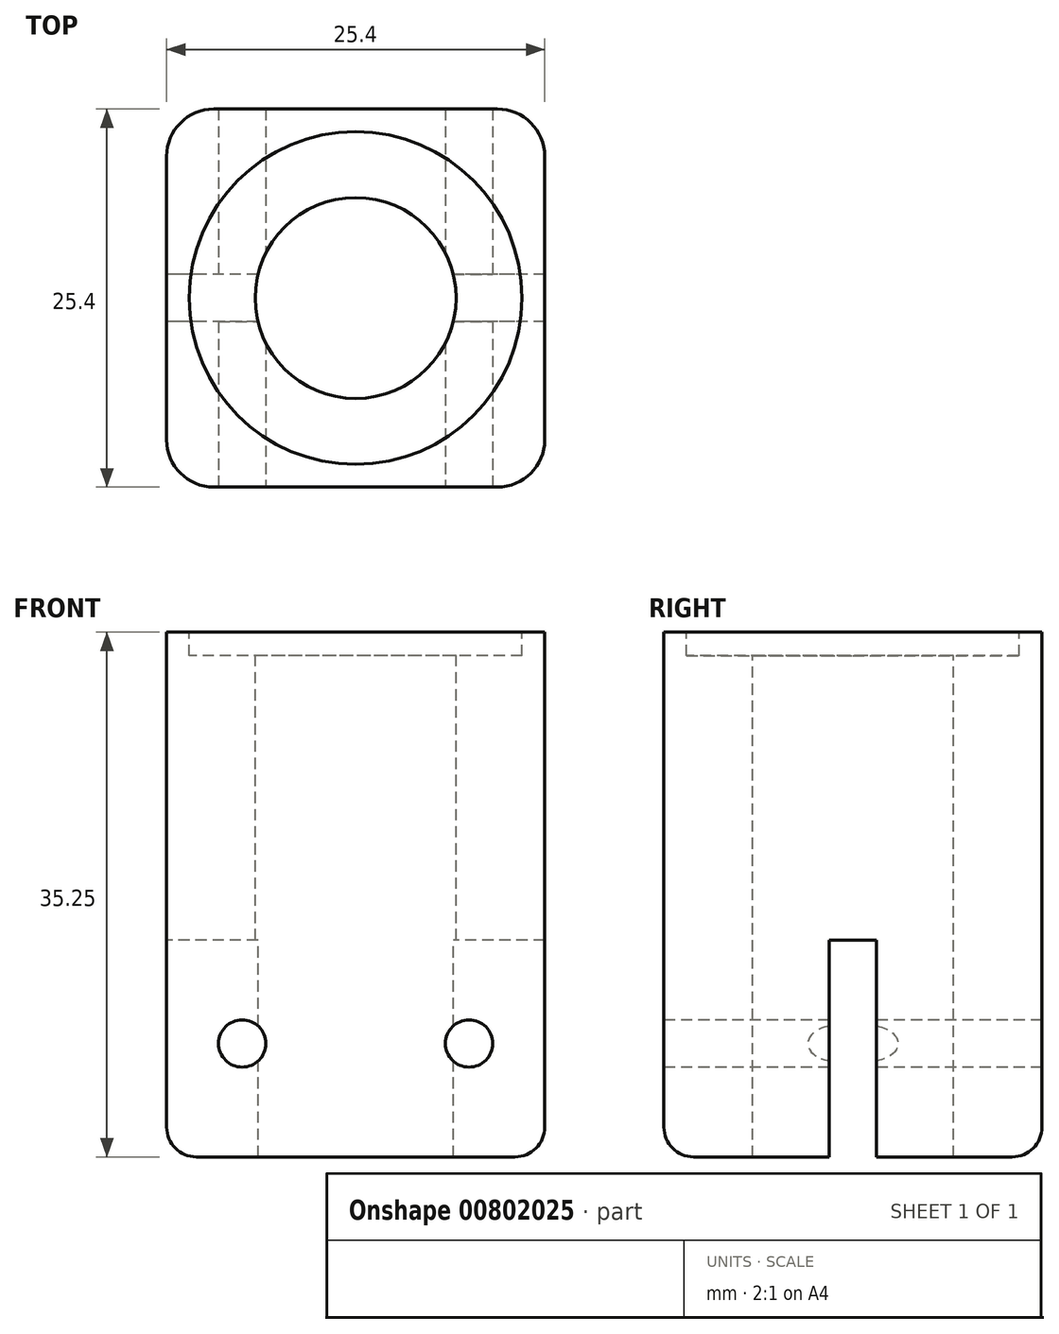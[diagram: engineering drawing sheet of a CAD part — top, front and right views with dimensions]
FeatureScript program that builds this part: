
annotation { "Feature Type Name" : "Feature", "Feature Type Description" : "" }
export const myFeature = defineFeature(function(context is Context, id is Id, definition is map)
    precondition{}
    {
        {
            var Q0;
            Q0=qCreatedBy(makeId("Top.planeOp"),FACE);
            var sketch = newSketch(context, id + "F0", { "sketchPlane" : qUnion([Q0])});
            skLineSegment(sketch, "E0.bottom", {"start": v(-9.52, 12.7) * mm, "end": v(9.52, 12.7) * mm});
            skLineSegment(sketch, "E0.top", {"start": v(-9.52, -12.7) * mm, "end": v(9.52, -12.7) * mm});
            skLineSegment(sketch, "E0.left", {"start": v(-12.7, 9.52) * mm, "end": v(-12.7, -9.53) * mm});
            skLineSegment(sketch, "E0.right", {"start": v(12.7, 9.52) * mm, "end": v(12.7, -9.53) * mm});
            skPoint(sketch, "E1.visualSharp", {"position": v(-12.7, 12.7) * mm});
            skArc(sketch, "E1.filletArc", {"start": v(-9.52, 12.7) * mm, "mid": v(-11.77, 11.77) * mm, "end": v(-12.7, 9.52) * mm});
            skPoint(sketch, "E2.visualSharp", {"position": v(12.7, 12.7) * mm});
            skArc(sketch, "E2.filletArc", {"start": v(12.7, 9.52) * mm, "mid": v(11.77, 11.77) * mm, "end": v(9.52, 12.7) * mm});
            skPoint(sketch, "E3.visualSharp", {"position": v(12.7, -12.7) * mm});
            skArc(sketch, "E3.filletArc", {"start": v(9.52, -12.7) * mm, "mid": v(11.77, -11.77) * mm, "end": v(12.7, -9.53) * mm});
            skPoint(sketch, "E4.visualSharp", {"position": v(-12.7, -12.7) * mm});
            skArc(sketch, "E4.filletArc", {"start": v(-12.7, -9.53) * mm, "mid": v(-11.77, -11.77) * mm, "end": v(-9.52, -12.7) * mm});
            skSolve(sketch);
        }
        {
            var Q0;
            Q0=qSketchRegion(id+"F0",true);
            extrude(context, id + "F1", {"entities" : qUnion([Q0]), "depth" : 36.1 * mm});
        }
        {
            var Q0;
            Q0=makeQuery(id+"F1.opExtrude","CAP_FACE",FACE,{"disambiguationData":[OSD([sQuery(id+"F0.wireOp",EDGE,"E0.bottom"),sQuery(id+"F0.wireOp",EDGE,"E0.top"),sQuery(id+"F0.wireOp",EDGE,"E0.left"),sQuery(id+"F0.wireOp",EDGE,"E0.right"),sQuery(id+"F0.wireOp",EDGE,"E1.filletArc"),sQuery(id+"F0.wireOp",EDGE,"E2.filletArc"),sQuery(id+"F0.wireOp",EDGE,"E3.filletArc"),sQuery(id+"F0.wireOp",EDGE,"E4.filletArc")])],"isStart":false});
            var sketch = newSketch(context, id + "F2", { "sketchPlane" : qUnion([Q0])});
            skPoint(sketch, "E5", {"position": v(0, 0) * mm});
            skSolve(sketch);
        }
        {
            var Q0;
            Q0=sQuery(id+"F2.wireOp",VERTEX,"E5");
            var Q1;
            Q1=makeQuery(id+"F1.opExtrude","SWEPT_BODY",BODY,{"disambiguationData":[OSD([sQuery(id+"F0.wireOp",EDGE,"E0.bottom"),sQuery(id+"F0.wireOp",EDGE,"E0.top"),sQuery(id+"F0.wireOp",EDGE,"E0.left"),sQuery(id+"F0.wireOp",EDGE,"E0.right"),sQuery(id+"F0.wireOp",EDGE,"E1.filletArc"),sQuery(id+"F0.wireOp",EDGE,"E2.filletArc"),sQuery(id+"F0.wireOp",EDGE,"E3.filletArc"),sQuery(id+"F0.wireOp",EDGE,"E4.filletArc")])]});
            hole(context, id + "F3", {"style" : HoleStyle.SIMPLE, "endStyle" : HoleEndStyle.THROUGH, "standardTappedOrClearance" : lookupTablePath({ "standard" : "ANSI", "engagement" : "75%", "pitch" : "11 tpi", "size" : "5/8", "type" : "Tapped" }), "standardBlindInLast" : lookupTablePath({ "standard" : "ANSI", "engagement" : "75%", "pitch" : "11 tpi", "size" : "5/8", "type" : "Tapped" }), "holeDiameter" : 13.5 * mm, "showTappedDepth" : true, "tappedDepth" : 19.05 * mm, "tapClearance" : 3, "startFromSketch" : true, "locations" : qUnion([Q0]), "scope" : qUnion([Q1]), "majorDiameter" : 15.88 * mm});
        }
        {
            var Q0;
            Q0=makeQuery(id+"F1.opExtrude","CAP_FACE",FACE,{"disambiguationData":[OSD([sQuery(id+"F0.wireOp",EDGE,"E0.bottom"),sQuery(id+"F0.wireOp",EDGE,"E0.top"),sQuery(id+"F0.wireOp",EDGE,"E0.left"),sQuery(id+"F0.wireOp",EDGE,"E0.right"),sQuery(id+"F0.wireOp",EDGE,"E1.filletArc"),sQuery(id+"F0.wireOp",EDGE,"E2.filletArc"),sQuery(id+"F0.wireOp",EDGE,"E3.filletArc"),sQuery(id+"F0.wireOp",EDGE,"E4.filletArc")])],"isStart":false});
            var sketch = newSketch(context, id + "F4", { "sketchPlane" : qUnion([Q0])});
            skCircle(sketch, "E6", {"center": v(0, 0) * mm, "radius": 11.18 * mm});
            skSolve(sketch);
        }
        {
            var Q0;
            Q0=qSketchRegion(id+"F4",true);
            extrude(context, id + "F5", {"entities" : qUnion([Q0]), "operationType" : NewBodyOperationType.REMOVE, "oppositeDirection" : true, "depth" : 1.59 * mm});
        }
        {
            var Q0;
            Q0=makeQuery(id+"F1.opExtrude","SWEPT_FACE",FACE,{"disambiguationData":[OSD([sQuery(id+"F0.wireOp",EDGE,"E0.left")])]});
            var sketch = newSketch(context, id + "F6", { "sketchPlane" : qUnion([Q0])});
            skLineSegment(sketch, "E7", {"start": v(0, 0) * mm, "end": v(0, 15.46) * mm, "construction": true});
            skPoint(sketch, "E8", {"position": v(0, 15.46) * mm});
            skLineSegment(sketch, "E9", {"start": v(0, 15.46) * mm, "end": v(1.59, 15.46) * mm});
            skLineSegment(sketch, "E10", {"start": v(1.59, 15.46) * mm, "end": v(1.59, -1.38) * mm});
            skLineSegment(sketch, "E11", {"start": v(0, 15.46) * mm, "end": v(-1.59, 15.46) * mm});
            skLineSegment(sketch, "E12", {"start": v(-1.59, 15.46) * mm, "end": v(-1.59, -0.8) * mm});
            skLineSegment(sketch, "E13", {"start": v(-1.59, -0.8) * mm, "end": v(1.59, -1.38) * mm});
            skSolve(sketch);
        }
        {
            var Q0;
            Q0=qSketchRegion(id+"F6",true);
            extrude(context, id + "F7", {"entities" : qUnion([Q0]), "operationType" : NewBodyOperationType.REMOVE, "endBound" : BoundingType.THROUGH_ALL, "oppositeDirection" : true, "depth" : 25.4 * mm});
        }
        {
            var Q0;
            Q0=makeQuery(id+"F1.opExtrude","SWEPT_FACE",FACE,{"disambiguationData":[OSD([sQuery(id+"F0.wireOp",EDGE,"E0.top")])]});
            var sketch = newSketch(context, id + "F8", { "sketchPlane" : qUnion([Q0])});
            skCircle(sketch, "E14", {"center": v(-7.62, 7.62) * mm, "radius": 1.59 * mm});
            skCircle(sketch, "E15", {"center": v(7.62, 7.62) * mm, "radius": 1.59 * mm});
            skSolve(sketch);
        }
        {
            var Q0;
            Q0=qSketchRegion(id+"F8",true);
            extrude(context, id + "F9", {"entities" : qUnion([Q0]), "operationType" : NewBodyOperationType.REMOVE, "endBound" : BoundingType.THROUGH_ALL, "oppositeDirection" : true, "depth" : 25.4 * mm});
        }
        {
            var Q0;
            {var subQ0=sQuery(id+"F0.wireOp",EDGE,"E1.filletArc");var subQ1=sQuery(id+"F0.wireOp",EDGE,"E0.left");Q0=makeQuery(id+"F7.boolean.opBoolean","SPLIT",EDGE,{"disambiguationData":[TD([makeQuery(id+"F1.opExtrude","SWEPT_FACE",FACE,{"disambiguationData":[OSD([subQ0])]})])],"derivedFrom":makeQuery(id+"F1.opExtrude","CAP_EDGE",EDGE,{"disambiguationData":[OSD([subQ1])],"isStart":true})});}
            var Q1;
            {var subQ0=sQuery(id+"F0.wireOp",EDGE,"E4.filletArc");var subQ1=sQuery(id+"F0.wireOp",EDGE,"E0.left");Q1=makeQuery(id+"F7.boolean.opBoolean","SPLIT",EDGE,{"disambiguationData":[TD([makeQuery(id+"F1.opExtrude","SWEPT_FACE",FACE,{"disambiguationData":[OSD([subQ0])]})])],"derivedFrom":makeQuery(id+"F1.opExtrude","CAP_EDGE",EDGE,{"disambiguationData":[OSD([subQ1])],"isStart":true})});}
            fillet(context, id + "F10", {"entities" : qUnion([Q0, Q1]), "radius" : 2 * mm, "tangentPropagation" : true, "allowEdgeOverflow" : false});
        }
        {
            var Q0;
            Q0=makeQuery(id+"F1.opExtrude","CAP_FACE",FACE,{"disambiguationData":[OSD([sQuery(id+"F0.wireOp",EDGE,"E0.bottom"),sQuery(id+"F0.wireOp",EDGE,"E0.top"),sQuery(id+"F0.wireOp",EDGE,"E0.left"),sQuery(id+"F0.wireOp",EDGE,"E0.right"),sQuery(id+"F0.wireOp",EDGE,"E1.filletArc"),sQuery(id+"F0.wireOp",EDGE,"E2.filletArc"),sQuery(id+"F0.wireOp",EDGE,"E3.filletArc"),sQuery(id+"F0.wireOp",EDGE,"E4.filletArc")])],"isStart":false});
            extrude(context, id + "F11", {"entities" : qUnion([Q0]), "operationType" : NewBodyOperationType.REMOVE, "oppositeDirection" : true, "depth" : .845 * mm});
        }
        {
            var Q0;
            Q0=makeQuery(id+"F5.boolean.opBoolean","COPY",FACE,{"derivedFrom":makeQuery(id+"F5.opExtrude","CAP_FACE",FACE,{"disambiguationData":[OSD([sQuery(id+"F4.wireOp",EDGE,"E6")])],"isStart":false})});
            extrude(context, id + "F12", {"entities" : qUnion([Q0]), "operationType" : NewBodyOperationType.REMOVE, "oppositeDirection" : true, "depth" : .845 * mm});
        }
        {
            var Q0;
            Q0=makeQuery(id+"F7.boolean.opBoolean","COPY",FACE,{"disambiguationData":[TD([makeQuery(id+"F1.opExtrude","SWEPT_FACE",FACE,{"disambiguationData":[OSD([sQuery(id+"F0.wireOp",EDGE,"E0.right")])]})])],"derivedFrom":makeQuery(id+"F7.opExtrude","SWEPT_FACE",FACE,{"disambiguationData":[OSD([sQuery(id+"F6.wireOp",EDGE,"E9"),sQuery(id+"F6.wireOp",EDGE,"E11")])]})});
            var Q1;
            Q1=makeQuery(id+"F7.boolean.opBoolean","COPY",FACE,{"disambiguationData":[TD([makeQuery(id+"F1.opExtrude","SWEPT_FACE",FACE,{"disambiguationData":[OSD([sQuery(id+"F0.wireOp",EDGE,"E0.left")])]})])],"derivedFrom":makeQuery(id+"F7.opExtrude","SWEPT_FACE",FACE,{"disambiguationData":[OSD([sQuery(id+"F6.wireOp",EDGE,"E9"),sQuery(id+"F6.wireOp",EDGE,"E11")])]})});
            extrude(context, id + "F13", {"entities" : qUnion([Q0, Q1]), "operationType" : NewBodyOperationType.ADD, "depth" : .889 * mm});
        }
    });
